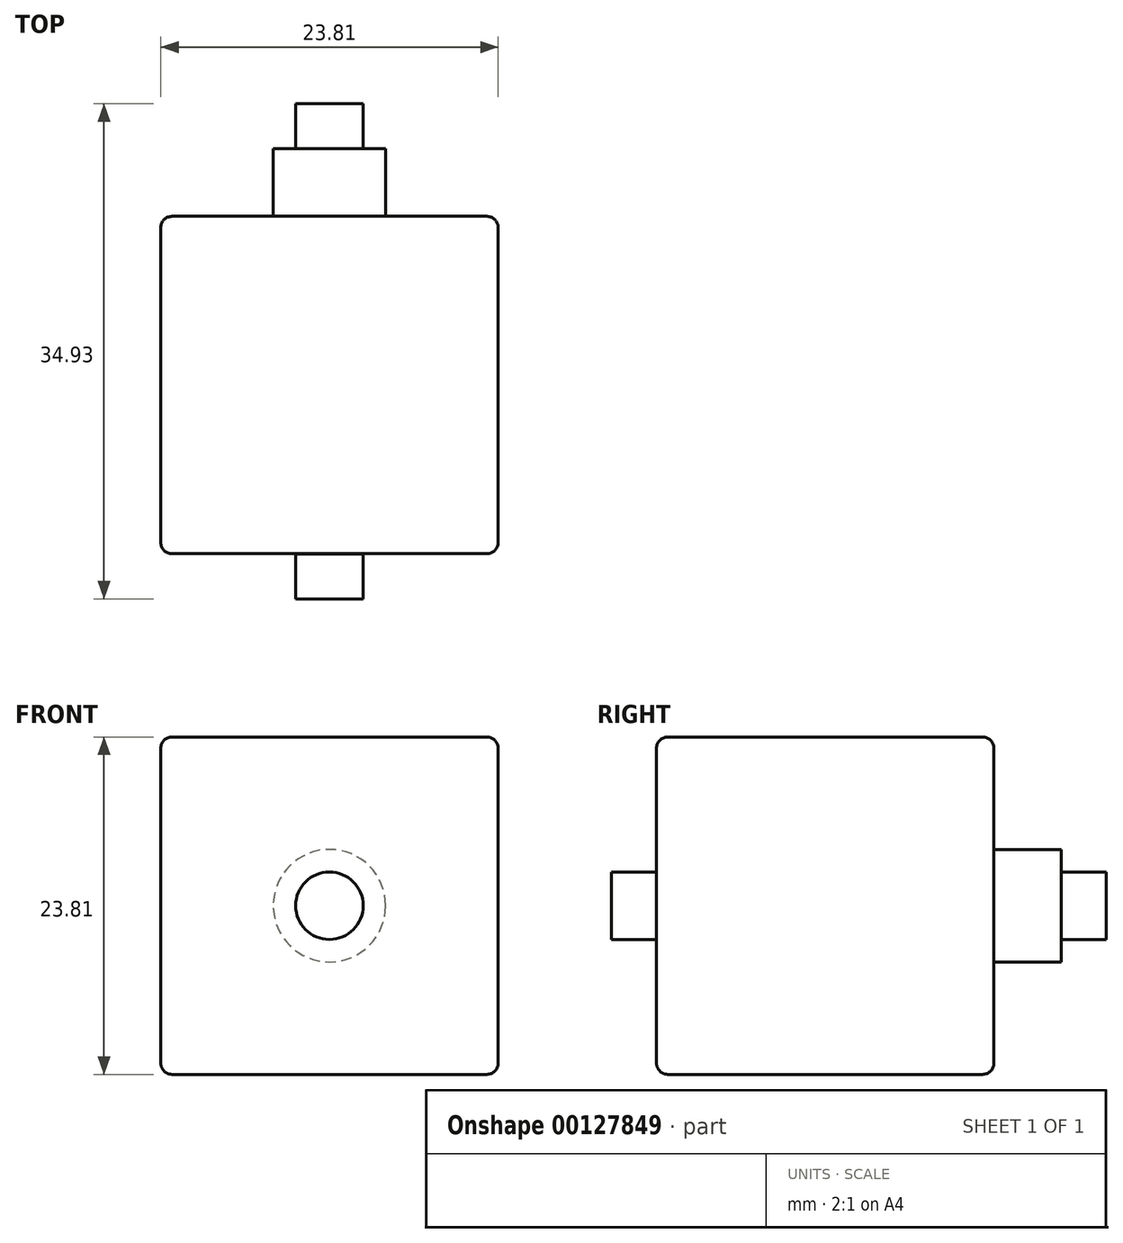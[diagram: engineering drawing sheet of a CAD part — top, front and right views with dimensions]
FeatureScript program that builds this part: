
annotation { "Feature Type Name" : "Feature", "Feature Type Description" : "" }
export const myFeature = defineFeature(function(context is Context, id is Id, definition is map)
    precondition{}
    {
        {
            var Q0;
            Q0=qCreatedBy(makeId("Top.planeOp"),FACE);
            var sketch = newSketch(context, id + "F0", { "sketchPlane" : qUnion([Q0])});
            skLineSegment(sketch, "E0.bottom", {"start": v(-14.78, 9.87) * mm, "end": v(9.03, 9.87) * mm});
            skLineSegment(sketch, "E0.top", {"start": v(-14.78, -13.94) * mm, "end": v(9.03, -13.94) * mm});
            skLineSegment(sketch, "E0.left", {"start": v(-14.78, 9.87) * mm, "end": v(-14.78, -13.94) * mm});
            skLineSegment(sketch, "E0.right", {"start": v(9.03, 9.87) * mm, "end": v(9.03, -13.94) * mm});
            skSolve(sketch);
        }
        {
            var Q0;
            Q0=makeQuery(id+"F0.imprint","IMPRINT",FACE,{"disambiguationData":[TD([[makeQuery(id+"F0.imprint","IMPRINT",EDGE,{"derivedFrom":sQuery(id+"F0.wireOp",EDGE,"E0.bottom")}),-1.0]])]});
            extrude(context, id + "F1", {"entities" : qUnion([Q0]), "depth" : 23.8 * mm});
        }
        {
            var Q0;
            Q0=makeQuery(id+"F1.opExtrude","SWEPT_FACE",FACE,{"disambiguationData":[OSD([sQuery(id+"F0.wireOp",EDGE,"E0.top")])]});
            cPlane(context, id + "F2", {"entities" : qUnion([Q0]), "cplaneType" : CPlaneType.OFFSET, "offset" : 2.5 / 406.4 * mm, "width" : 152.4 * mm, "height" : 152.4 * mm});
        }
        {
            var Q0;
            Q0=qCreatedBy(id+"F2.planeOp",FACE);
            var sketch = newSketch(context, id + "F3", { "sketchPlane" : qUnion([Q0])});
            skCircle(sketch, "E1", {"center": v(-2.88, 11.9) * mm, "radius": 3.97 * mm});
            skSolve(sketch);
        }
        {
            var Q0;
            Q0=sQuery(id+"F3.wireOp",EDGE,"E1");
            extrude(context, id + "F4", {"bodyType" : ToolBodyType.SURFACE, "surfaceEntities" : qUnion([Q0]), "oppositeDirection" : true, "depth" : 4.76 * mm});
        }
        {
            var Q0;
            Q0=qCreatedBy(id+"F2.planeOp",FACE);
            cPlane(context, id + "F5", {"entities" : qUnion([Q0]), "cplaneType" : CPlaneType.OFFSET, "offset" : 3.17 * mm, "width" : 152.4 * mm, "height" : 152.4 * mm});
        }
        {
            var Q0;
            Q0=qCreatedBy(id+"F5.planeOp",FACE);
            var sketch = newSketch(context, id + "F6", { "sketchPlane" : qUnion([Q0])});
            skCircle(sketch, "E2", {"center": v(-2.88, 11.9) * mm, "radius": 2.38 * mm});
            skSolve(sketch);
        }
        {
            var Q0;
            Q0=makeQuery(id+"F6.imprint","IMPRINT",FACE,{"disambiguationData":[TD([[makeQuery(id+"F6.imprint","IMPRINT",EDGE,{"derivedFrom":sQuery(id+"F6.wireOp",EDGE,"E2")}),1.0]])]});
            extrude(context, id + "F7", {"entities" : qUnion([Q0]), "oppositeDirection" : true, "depth" : 3.17 * mm});
        }
        {
            var Q0;
            Q0=makeQuery(id+"F1.opExtrude","SWEPT_FACE",FACE,{"disambiguationData":[OSD([sQuery(id+"F0.wireOp",EDGE,"E0.bottom")])]});
            cPlane(context, id + "F8", {"entities" : qUnion([Q0]), "cplaneType" : CPlaneType.OFFSET, "offset" : 4.76 * mm, "width" : 152.4 * mm, "height" : 152.4 * mm});
        }
        {
            var Q0;
            Q0=qCreatedBy(id+"F8.planeOp",FACE);
            var sketch = newSketch(context, id + "F9", { "sketchPlane" : qUnion([Q0])});
            skCircle(sketch, "E3", {"center": v(2.88, 11.9) * mm, "radius": 3.97 * mm});
            skSolve(sketch);
        }
        {
            var Q0;
            Q0=makeQuery(id+"F9.imprint","IMPRINT",FACE,{"disambiguationData":[TD([[makeQuery(id+"F9.imprint","IMPRINT",EDGE,{"derivedFrom":sQuery(id+"F9.wireOp",EDGE,"E3")}),1.0]])]});
            extrude(context, id + "F10", {"entities" : qUnion([Q0]), "operationType" : NewBodyOperationType.ADD, "oppositeDirection" : true, "depth" : 4.76 * mm});
        }
        {
            var Q0;
            Q0=qCreatedBy(id+"F8.planeOp",FACE);
            cPlane(context, id + "F11", {"entities" : qUnion([Q0]), "cplaneType" : CPlaneType.OFFSET, "offset" : 3.17 * mm, "width" : 152.4 * mm, "height" : 152.4 * mm});
        }
        {
            var Q0;
            Q0=qCreatedBy(id+"F11.planeOp",FACE);
            var sketch = newSketch(context, id + "F12", { "sketchPlane" : qUnion([Q0])});
            skCircle(sketch, "E4", {"center": v(2.88, 11.9) * mm, "radius": 2.38 * mm});
            skSolve(sketch);
        }
        {
            var Q0;
            Q0=makeQuery(id+"F12.imprint","IMPRINT",FACE,{"disambiguationData":[TD([[makeQuery(id+"F12.imprint","IMPRINT",EDGE,{"derivedFrom":sQuery(id+"F12.wireOp",EDGE,"E4")}),1.0]])]});
            extrude(context, id + "F13", {"entities" : qUnion([Q0]), "operationType" : NewBodyOperationType.ADD, "oppositeDirection" : true, "depth" : 3.17 * mm});
        }
        {
            var Q0;
            Q0=makeQuery(id+"F1.opExtrude","CAP_EDGE",EDGE,{"disambiguationData":[OSD([sQuery(id+"F0.wireOp",EDGE,"E0.right")])],"isStart":true});
            var Q1;
            Q1=makeQuery(id+"F1.opExtrude","CAP_EDGE",EDGE,{"disambiguationData":[OSD([sQuery(id+"F0.wireOp",EDGE,"E0.right")])],"isStart":false});
            var Q2;
            Q2=makeQuery(id+"F1.opExtrude","SWEPT_EDGE",EDGE,{"disambiguationData":[OSD([sQuery(id+"F0.wireOp",EDGE,"E0.top"),sQuery(id+"F0.wireOp",EDGE,"E0.right")])]});
            var Q3;
            Q3=makeQuery(id+"F1.opExtrude","SWEPT_EDGE",EDGE,{"disambiguationData":[OSD([sQuery(id+"F0.wireOp",EDGE,"E0.bottom"),sQuery(id+"F0.wireOp",EDGE,"E0.right")])]});
            var Q4;
            Q4=makeQuery(id+"F1.opExtrude","CAP_EDGE",EDGE,{"disambiguationData":[OSD([sQuery(id+"F0.wireOp",EDGE,"E0.bottom")])],"isStart":false});
            var Q5;
            Q5=makeQuery(id+"F1.opExtrude","CAP_EDGE",EDGE,{"disambiguationData":[OSD([sQuery(id+"F0.wireOp",EDGE,"E0.left")])],"isStart":false});
            var Q6;
            Q6=makeQuery(id+"F1.opExtrude","CAP_EDGE",EDGE,{"disambiguationData":[OSD([sQuery(id+"F0.wireOp",EDGE,"E0.top")])],"isStart":false});
            var Q7;
            Q7=makeQuery(id+"F1.opExtrude","CAP_EDGE",EDGE,{"disambiguationData":[OSD([sQuery(id+"F0.wireOp",EDGE,"E0.bottom")])],"isStart":true});
            var Q8;
            Q8=makeQuery(id+"F1.opExtrude","SWEPT_EDGE",EDGE,{"disambiguationData":[OSD([sQuery(id+"F0.wireOp",EDGE,"E0.bottom"),sQuery(id+"F0.wireOp",EDGE,"E0.left")])]});
            var Q9;
            Q9=makeQuery(id+"F1.opExtrude","SWEPT_EDGE",EDGE,{"disambiguationData":[OSD([sQuery(id+"F0.wireOp",EDGE,"E0.top"),sQuery(id+"F0.wireOp",EDGE,"E0.left")])]});
            var Q10;
            Q10=makeQuery(id+"F1.opExtrude","CAP_EDGE",EDGE,{"disambiguationData":[OSD([sQuery(id+"F0.wireOp",EDGE,"E0.top")])],"isStart":true});
            var Q11;
            Q11=makeQuery(id+"F1.opExtrude","CAP_EDGE",EDGE,{"disambiguationData":[OSD([sQuery(id+"F0.wireOp",EDGE,"E0.left")])],"isStart":true});
            fillet(context, id + "F14", {"entities" : qUnion([Q0, Q1, Q2, Q3, Q4, Q5, Q6, Q7, Q8, Q9, Q10, Q11]), "radius" : 0.8 * mm, "tangentPropagation" : true, "allowEdgeOverflow" : false});
        }
    });
